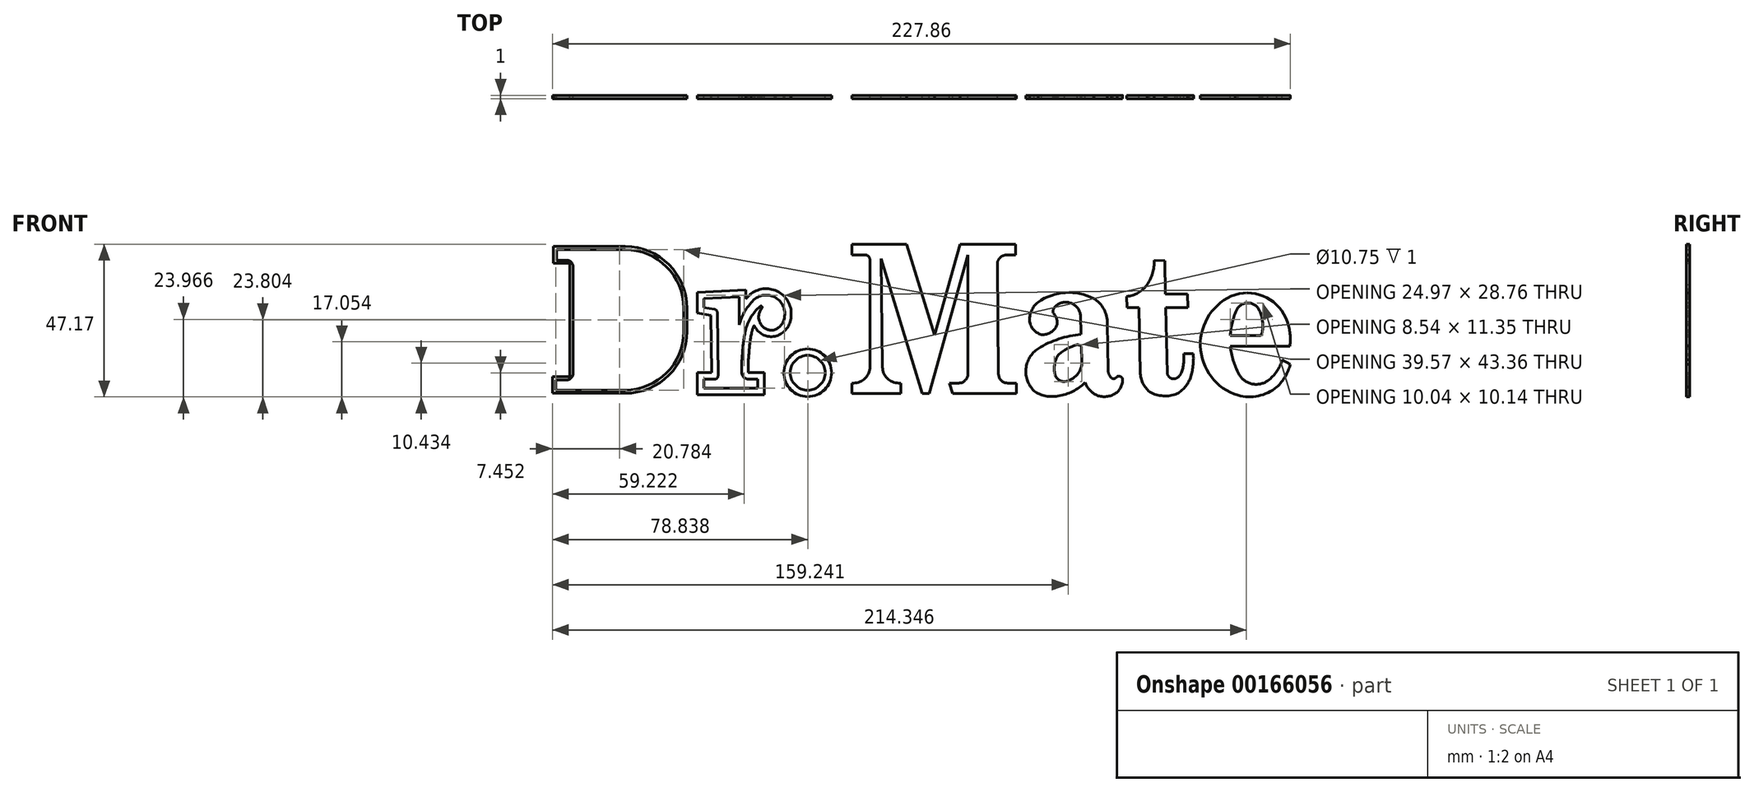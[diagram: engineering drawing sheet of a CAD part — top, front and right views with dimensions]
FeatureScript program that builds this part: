
annotation { "Feature Type Name" : "Feature", "Feature Type Description" : "" }
export const myFeature = defineFeature(function(context is Context, id is Id, definition is map)
    precondition{}
    {
        {
            var Q0;
            Q0=qCreatedBy(makeId("Front.planeOp"),FACE);
            var sketch = newSketch(context, id + "F0", { "sketchPlane" : qUnion([Q0])});
            skLineSegment(sketch, "E0", {"start": v(23.83, 45.48) * mm, "end": v(2.7, 45.48) * mm});
            skLineSegment(sketch, "E1", {"start": v(2.7, 45.48) * mm, "end": v(2.7, 42.24) * mm});
            skLineSegment(sketch, "E2", {"start": v(2.7, 42.24) * mm, "end": v(5.73, 42.24) * mm});
            skLineSegment(sketch, "E3", {"start": v(7.73, 40.24) * mm, "end": v(7.73, 7.24) * mm});
            skLineSegment(sketch, "E4", {"start": v(5.73, 5.24) * mm, "end": v(2.36, 5.24) * mm});
            skLineSegment(sketch, "E5", {"start": v(2.36, 5.24) * mm, "end": v(2.36, 2.11) * mm});
            skLineSegment(sketch, "E6", {"start": v(2.36, 2.11) * mm, "end": v(23.83, 2.11) * mm});
            skPoint(sketch, "E7.visualSharp", {"position": v(7.73, 42.24) * mm});
            skArc(sketch, "E7.filletArc", {"start": v(7.73, 40.24) * mm, "mid": v(7.14, 41.66) * mm, "end": v(5.73, 42.24) * mm});
            skPoint(sketch, "E8.visualSharp", {"position": v(7.73, 5.24) * mm});
            skArc(sketch, "E8.filletArc", {"start": v(5.73, 5.24) * mm, "mid": v(7.14, 5.83) * mm, "end": v(7.73, 7.24) * mm});
            skLineSegment(sketch, "E9", {"start": v(41.93, 27.38) * mm, "end": v(41.93, 20.21) * mm});
            skPoint(sketch, "E10.visualSharp", {"position": v(41.93, 45.48) * mm});
            skArc(sketch, "E10.filletArc", {"start": v(41.93, 27.38) * mm, "mid": v(36.63, 40.17) * mm, "end": v(23.83, 45.48) * mm});
            skPoint(sketch, "E11.visualSharp", {"position": v(41.93, 2.11) * mm});
            skArc(sketch, "E11.filletArc", {"start": v(23.83, 2.11) * mm, "mid": v(36.63, 7.41) * mm, "end": v(41.93, 20.21) * mm});
            skSolve(sketch);
        }
        {
            var Q0;
            Q0=qSketchRegion(id+"F0",true);
            extrude(context, id + "F1", {"entities" : qUnion([Q0]), "endBound" : BoundingType.SYMMETRIC, "depth" : 10 * mm});
        }
        {
            var Q0;
            Q0=qCreatedBy(makeId("Front.planeOp"),FACE);
            var sketch = newSketch(context, id + "F2", { "sketchPlane" : qUnion([Q0])});
            skLineSegment(sketch, "E12", {"start": v(20.26, 40.33) * mm, "end": v(20.26, 7.37) * mm});
            skLineSegment(sketch, "E13", {"start": v(22.26, 5.37) * mm, "end": v(23.68, 5.37) * mm});
            skLineSegment(sketch, "E14", {"start": v(22.26, 42.33) * mm, "end": v(23.68, 42.33) * mm});
            skPoint(sketch, "E15.visualSharp", {"position": v(20.26, 42.33) * mm});
            skArc(sketch, "E15.filletArc", {"start": v(22.26, 42.33) * mm, "mid": v(20.84, 41.75) * mm, "end": v(20.26, 40.33) * mm});
            skPoint(sketch, "E16.visualSharp", {"position": v(20.26, 5.37) * mm});
            skArc(sketch, "E16.filletArc", {"start": v(20.26, 7.37) * mm, "mid": v(20.84, 5.96) * mm, "end": v(22.26, 5.37) * mm});
            skPoint(sketch, "E17.visualSharp", {"position": v(41.68, 42.33) * mm});
            skArc(sketch, "E17.filletArc", {"start": v(29.92, 41.22) * mm, "mid": v(26.85, 42.05) * mm, "end": v(23.68, 42.33) * mm});
            skPoint(sketch, "E18.visualSharp", {"position": v(41.68, 5.37) * mm});
            skArc(sketch, "E18.filletArc", {"start": v(23.68, 5.37) * mm, "mid": v(26.85, 5.66) * mm, "end": v(29.92, 6.49) * mm});
            skArc(sketch, "E19", {"start": v(29.92, 6.49) * mm, "mid": v(31.56, 8.17) * mm, "end": v(33.02, 10) * mm});
            skArc(sketch, "E20.trimOffspring", {"start": v(33.02, 37.7) * mm, "mid": v(31.56, 39.54) * mm, "end": v(29.92, 41.22) * mm});
            skArc(sketch, "E21", {"start": v(33.02, 10) * mm, "mid": v(35.84, 23.85) * mm, "end": v(33.02, 37.7) * mm});
            skSolve(sketch);
        }
        {
            var Q0;
            Q0=qSketchRegion(id+"F2",true);
            extrude(context, id + "F3", {"entities" : qUnion([Q0]), "operationType" : NewBodyOperationType.REMOVE, "endBound" : BoundingType.SYMMETRIC, "oppositeDirection" : true, "depth" : 25 * mm});
        }
        {
            var Q0;
            Q0=makeQuery(id+"F3.boolean.opBoolean","COPY",EDGE,{"derivedFrom":makeQuery(id+"F3.opExtrude","SWEPT_EDGE",EDGE,{"disambiguationData":[OSD([sQuery(id+"F2.wireOp",EDGE,"E19"),sQuery(id+"F2.wireOp",EDGE,"E21")])]})});
            var Q1;
            Q1=makeQuery(id+"F3.boolean.opBoolean","COPY",EDGE,{"derivedFrom":makeQuery(id+"F3.opExtrude","SWEPT_EDGE",EDGE,{"disambiguationData":[OSD([sQuery(id+"F2.wireOp",EDGE,"E18.filletArc"),sQuery(id+"F2.wireOp",EDGE,"E19")])]})});
            var Q2;
            Q2=makeQuery(id+"F3.boolean.opBoolean","COPY",EDGE,{"derivedFrom":makeQuery(id+"F3.opExtrude","SWEPT_EDGE",EDGE,{"disambiguationData":[OSD([sQuery(id+"F2.wireOp",EDGE,"E20.trimOffspring"),sQuery(id+"F2.wireOp",EDGE,"E21")])]})});
            var Q3;
            Q3=makeQuery(id+"F3.boolean.opBoolean","COPY",EDGE,{"derivedFrom":makeQuery(id+"F3.opExtrude","SWEPT_EDGE",EDGE,{"disambiguationData":[OSD([sQuery(id+"F2.wireOp",EDGE,"E17.filletArc"),sQuery(id+"F2.wireOp",EDGE,"E20.trimOffspring")])]})});
            fillet(context, id + "F4", {"entities" : qUnion([Q0, Q1, Q2, Q3]), "radius" : 5 * mm, "tangentPropagation" : true, "allowEdgeOverflow" : false});
        }
        {
            var Q0;
            Q0=qCreatedBy(makeId("Front.planeOp"),FACE);
            var sketch = newSketch(context, id + "F5", { "sketchPlane" : qUnion([Q0])});
            skLineSegment(sketch, "E22", {"start": v(48.1, 30.42) * mm, "end": v(48.1, 27.61) * mm});
            skLineSegment(sketch, "E23", {"start": v(48.1, 30.42) * mm, "end": v(59.09, 30.93) * mm});
            skLineSegment(sketch, "E24", {"start": v(48.1, 2.66) * mm, "end": v(64.8, 2.66) * mm});
            skLineSegment(sketch, "E25", {"start": v(59.09, 30.93) * mm, "end": v(59.09, 22.2) * mm});
            skLineSegment(sketch, "E26", {"start": v(48.1, 5.47) * mm, "end": v(51.51, 5.47) * mm});
            skLineSegment(sketch, "E27", {"start": v(48.1, 27.61) * mm, "end": v(51.46, 27.04) * mm});
            skLineSegment(sketch, "E28", {"start": v(64.8, 5.47) * mm, "end": v(64.8, 2.66) * mm});
            skLineSegment(sketch, "E29.trimOffspring", {"start": v(52.29, 26.06) * mm, "end": v(52.51, 6.48) * mm});
            skLineSegment(sketch, "E30.trimOffspring", {"start": v(61.83, 5.47) * mm, "end": v(64.8, 5.47) * mm});
            skLineSegment(sketch, "E31.trimOffspring", {"start": v(48.1, 5.47) * mm, "end": v(48.1, 2.66) * mm});
            skArc(sketch, "E32", {"start": v(73.07, 24.94) * mm, "mid": v(70.3, 30.62) * mm, "end": v(64, 30.34) * mm});
            skArc(sketch, "E33", {"start": v(69.92, 20.7) * mm, "mid": v(72.14, 22.34) * mm, "end": v(73.07, 24.94) * mm});
            skArc(sketch, "E34", {"start": v(64, 30.34) * mm, "mid": v(60.9, 26.65) * mm, "end": v(59.09, 22.2) * mm});
            skArc(sketch, "E35", {"start": v(65.86, 22.25) * mm, "mid": v(67.65, 20.85) * mm, "end": v(69.92, 20.7) * mm});
            skArc(sketch, "E36", {"start": v(66.1, 27.52) * mm, "mid": v(65.06, 24.93) * mm, "end": v(65.86, 22.25) * mm});
            skArc(sketch, "E37", {"start": v(59.89, 6.98) * mm, "mid": v(60.62, 5.92) * mm, "end": v(61.83, 5.47) * mm});
            skArc(sketch, "E38", {"start": v(60.03, 13.08) * mm, "mid": v(59.8, 10.03) * mm, "end": v(59.89, 6.98) * mm});
            skArc(sketch, "E39", {"start": v(60.96, 20.37) * mm, "mid": v(60.34, 16.75) * mm, "end": v(60.03, 13.08) * mm});
            skArc(sketch, "E40", {"start": v(65.5, 27.94) * mm, "mid": v(62.63, 24.52) * mm, "end": v(60.96, 20.37) * mm});
            skArc(sketch, "E41", {"start": v(66.1, 27.52) * mm, "mid": v(65.98, 27.98) * mm, "end": v(65.5, 27.94) * mm});
            skPoint(sketch, "E42.visualSharp", {"position": v(52.28, 26.9) * mm});
            skArc(sketch, "E42.filletArc", {"start": v(52.29, 26.06) * mm, "mid": v(52.05, 26.7) * mm, "end": v(51.46, 27.04) * mm});
            skPoint(sketch, "E43.visualSharp", {"position": v(52.52, 5.47) * mm});
            skArc(sketch, "E43.filletArc", {"start": v(51.51, 5.47) * mm, "mid": v(52.22, 5.77) * mm, "end": v(52.51, 6.48) * mm});
            skSolve(sketch);
        }
        {
            var Q0;
            Q0=qSketchRegion(id+"F5",true);
            extrude(context, id + "F6", {"entities" : qUnion([Q0]), "endBound" : BoundingType.SYMMETRIC, "depth" : 10 * mm});
        }
        {
            var Q0;
            Q0=qCreatedBy(makeId("Front.planeOp"),FACE);
            var sketch = newSketch(context, id + "F7", { "sketchPlane" : qUnion([Q0])});
            skCircle(sketch, "E44", {"center": v(80.2, 7.44) * mm, "radius": 5.38 * mm});
            skSolve(sketch);
        }
        {
            var Q0;
            Q0=qSketchRegion(id+"F7",true);
            extrude(context, id + "F8", {"entities" : qUnion([Q0]), "endBound" : BoundingType.SYMMETRIC, "depth" : 10 * mm});
        }
        {
            var Q0;
            Q0=qCreatedBy(makeId("Front.planeOp"),FACE);
            var sketch = newSketch(context, id + "F9", { "sketchPlane" : qUnion([Q0])});
            skLineSegment(sketch, "E45", {"start": v(93.8, 47.16) * mm, "end": v(110.75, 47.16) * mm});
            skLineSegment(sketch, "E46", {"start": v(127.22, 47.16) * mm, "end": v(119.38, 19.02) * mm});
            skLineSegment(sketch, "E47", {"start": v(93.8, 47.16) * mm, "end": v(93.8, 43.88) * mm});
            skLineSegment(sketch, "E48", {"start": v(99.4, 42.37) * mm, "end": v(99.4, 9.27) * mm});
            skLineSegment(sketch, "E49", {"start": v(93.8, 1.02) * mm, "end": v(108.94, 1.02) * mm});
            skLineSegment(sketch, "E50", {"start": v(102.92, 42.74) * mm, "end": v(103.28, 9.22) * mm});
            skLineSegment(sketch, "E51", {"start": v(102.92, 42.74) * mm, "end": v(115.57, 1.02) * mm});
            skLineSegment(sketch, "E52", {"start": v(110.75, 47.16) * mm, "end": v(119.38, 19.02) * mm});
            skLineSegment(sketch, "E53", {"start": v(129.69, 43.89) * mm, "end": v(129.69, 7.07) * mm});
            skLineSegment(sketch, "E54", {"start": v(138.75, 40.98) * mm, "end": v(139.12, 7.04) * mm});
            skLineSegment(sketch, "E55", {"start": v(144.36, 47.16) * mm, "end": v(144.39, 43.8) * mm});
            skLineSegment(sketch, "E56", {"start": v(93.8, 43.88) * mm, "end": v(97.9, 43.87) * mm});
            skLineSegment(sketch, "E57.0", {"start": v(93.8, 4.27) * mm, "end": v(94.4, 4.27) * mm});
            skPoint(sketch, "E58.orphan", {"position": v(90.95, 43.89) * mm});
            skPoint(sketch, "E59.orphan", {"position": v(90.95, 47.16) * mm});
            skLineSegment(sketch, "E60.trimOffspring", {"start": v(144.68, 4.27) * mm, "end": v(144.7, 1.02) * mm});
            skLineSegment(sketch, "E61.trimOffspring", {"start": v(141.56, 43.8) * mm, "end": v(144.39, 43.8) * mm});
            skLineSegment(sketch, "E62.trimOffspring", {"start": v(127.22, 47.16) * mm, "end": v(144.36, 47.16) * mm});
            skLineSegment(sketch, "E63.trimOffspring", {"start": v(93.8, 4.27) * mm, "end": v(93.8, 1.02) * mm});
            skLineSegment(sketch, "E64.trimOffspring", {"start": v(117.74, 1.02) * mm, "end": v(129.69, 43.89) * mm});
            skLineSegment(sketch, "E65.trimOffspring", {"start": v(123.9, 4.27) * mm, "end": v(124.9, 1.02) * mm});
            skLineSegment(sketch, "E66.trimOffspring", {"start": v(108.28, 4.27) * mm, "end": v(108.96, 4.27) * mm});
            skLineSegment(sketch, "E67.trimOffspring", {"start": v(123.9, 4.27) * mm, "end": v(126.89, 4.27) * mm});
            skLineSegment(sketch, "E68.trimOffspring", {"start": v(124.9, 1.02) * mm, "end": v(144.7, 1.02) * mm});
            skLineSegment(sketch, "E69.trimOffspring", {"start": v(141.92, 4.27) * mm, "end": v(144.68, 4.27) * mm});
            skPoint(sketch, "E70.startSnap0", {"position": v(108.96, 4.27) * mm});
            skLineSegment(sketch, "E71", {"start": v(108.94, 4.27) * mm, "end": v(108.94, 1.02) * mm});
            skLineSegment(sketch, "E72.trimOffspring", {"start": v(115.57, 1.02) * mm, "end": v(117.74, 1.02) * mm});
            skPoint(sketch, "E73.visualSharp", {"position": v(99.4, 43.87) * mm});
            skArc(sketch, "E73.filletArc", {"start": v(99.4, 42.37) * mm, "mid": v(98.96, 43.43) * mm, "end": v(97.9, 43.87) * mm});
            skPoint(sketch, "E74.visualSharp", {"position": v(99.4, 4.27) * mm});
            skArc(sketch, "E74.filletArc", {"start": v(94.4, 4.27) * mm, "mid": v(97.94, 5.74) * mm, "end": v(99.4, 9.27) * mm});
            skPoint(sketch, "E75.visualSharp", {"position": v(103.34, 4.27) * mm});
            skArc(sketch, "E75.filletArc", {"start": v(103.28, 9.22) * mm, "mid": v(104.77, 5.72) * mm, "end": v(108.28, 4.27) * mm});
            skPoint(sketch, "E76.visualSharp", {"position": v(129.69, 4.27) * mm});
            skArc(sketch, "E76.filletArc", {"start": v(126.89, 4.27) * mm, "mid": v(128.87, 5.1) * mm, "end": v(129.69, 7.07) * mm});
            skPoint(sketch, "E77.visualSharp", {"position": v(139.15, 4.27) * mm});
            skArc(sketch, "E77.filletArc", {"start": v(139.12, 7.04) * mm, "mid": v(139.95, 5.08) * mm, "end": v(141.92, 4.27) * mm});
            skPoint(sketch, "E78.visualSharp", {"position": v(138.72, 43.81) * mm});
            skArc(sketch, "E78.filletArc", {"start": v(141.56, 43.8) * mm, "mid": v(139.56, 42.98) * mm, "end": v(138.75, 40.98) * mm});
            skSolve(sketch);
        }
        {
            var Q0;
            Q0=qSketchRegion(id+"F9",true);
            extrude(context, id + "F10", {"entities" : qUnion([Q0]), "endBound" : BoundingType.SYMMETRIC, "depth" : 1 * mm});
        }
        {
            var Q0;
            Q0=qCreatedBy(makeId("Front.planeOp"),FACE);
            var sketch = newSketch(context, id + "F11", { "sketchPlane" : qUnion([Q0])});
            skArc(sketch, "E79", {"start": v(172.7, 22.65) * mm, "mid": v(171.66, 27.12) * mm, "end": v(168.48, 30.43) * mm});
            skLineSegment(sketch, "E80", {"start": v(172.7, 22.65) * mm, "end": v(172.93, 8.42) * mm});
            skArc(sketch, "E81", {"start": v(168.48, 30.43) * mm, "mid": v(159.76, 32.2) * mm, "end": v(151.36, 29.26) * mm});
            skArc(sketch, "E82", {"start": v(151.36, 29.26) * mm, "mid": v(149.3, 26.59) * mm, "end": v(148.75, 23.26) * mm});
            skArc(sketch, "E83", {"start": v(148.75, 23.26) * mm, "mid": v(149.95, 20.7) * mm, "end": v(152.36, 19.26) * mm});
            skArc(sketch, "E84", {"start": v(152.36, 19.26) * mm, "mid": v(155.23, 19.9) * mm, "end": v(157.14, 22.15) * mm});
            skArc(sketch, "E85", {"start": v(157.14, 22.15) * mm, "mid": v(157.07, 24.2) * mm, "end": v(155.97, 25.93) * mm});
            skArc(sketch, "E86", {"start": v(156.97, 28.2) * mm, "mid": v(156.13, 27.22) * mm, "end": v(155.97, 25.93) * mm});
            skArc(sketch, "E87", {"start": v(164.45, 25.33) * mm, "mid": v(161.55, 28.93) * mm, "end": v(156.97, 28.2) * mm});
            skLineSegment(sketch, "E88", {"start": v(164.45, 25.33) * mm, "end": v(164.87, 11.05) * mm});
            skArc(sketch, "E89", {"start": v(164.74, 15.46) * mm, "mid": v(164.18, 15.94) * mm, "end": v(163.46, 16.1) * mm});
            skArc(sketch, "E90", {"start": v(164.63, 19.28) * mm, "mid": v(157.74, 17.88) * mm, "end": v(151.36, 14.93) * mm});
            skArc(sketch, "E91", {"start": v(151.36, 14.93) * mm, "mid": v(147.6, 8.68) * mm, "end": v(150.1, 1.82) * mm});
            skArc(sketch, "E92", {"start": v(150.1, 1.82) * mm, "mid": v(153.65, 0.29) * mm, "end": v(157.51, 0.28) * mm});
            skArc(sketch, "E93", {"start": v(157.51, 0.28) * mm, "mid": v(162.02, 1.68) * mm, "end": v(165.85, 4.44) * mm});
            skArc(sketch, "E94", {"start": v(159.52, 4.75) * mm, "mid": v(163.4, 6.87) * mm, "end": v(164.87, 11.05) * mm});
            skArc(sketch, "E95", {"start": v(156.5, 7.23) * mm, "mid": v(157.54, 5.41) * mm, "end": v(159.52, 4.75) * mm});
            skArc(sketch, "E96", {"start": v(157.54, 12.92) * mm, "mid": v(156.46, 10.18) * mm, "end": v(156.5, 7.23) * mm});
            skPoint(sketch, "E96.startSnap0", {"position": v(157.54, 5.41) * mm});
            skArc(sketch, "E97", {"start": v(163.46, 16.1) * mm, "mid": v(160.31, 14.86) * mm, "end": v(157.54, 12.92) * mm});
            skArc(sketch, "E98", {"start": v(172.93, 8.42) * mm, "mid": v(173.22, 7) * mm, "end": v(174.02, 5.8) * mm});
            skArc(sketch, "E99", {"start": v(174.02, 5.8) * mm, "mid": v(174.98, 5.66) * mm, "end": v(175.7, 6.3) * mm});
            skArc(sketch, "E100", {"start": v(177.42, 5.6) * mm, "mid": v(176.71, 6.32) * mm, "end": v(175.7, 6.3) * mm});
            skArc(sketch, "E101", {"start": v(174.62, 0.74) * mm, "mid": v(176.77, 2.73) * mm, "end": v(177.42, 5.6) * mm});
            skArc(sketch, "E102", {"start": v(165.85, 4.44) * mm, "mid": v(167.1, 2.35) * mm, "end": v(168.94, 0.77) * mm});
            skArc(sketch, "E103", {"start": v(168.94, 0.77) * mm, "mid": v(171.78, 0.05) * mm, "end": v(174.62, 0.74) * mm});
            skSolve(sketch);
        }
        {
            var Q0;
            Q0=qSketchRegion(id+"F11",true);
            extrude(context, id + "F12", {"entities" : qUnion([Q0]), "endBound" : BoundingType.SYMMETRIC, "depth" : 1 * mm});
        }
        {
            var Q0;
            Q0=qCreatedBy(makeId("Front.planeOp"),FACE);
            var sketch = newSketch(context, id + "F13", { "sketchPlane" : qUnion([Q0])});
            skLineSegment(sketch, "E104", {"start": v(187.18, 42.16) * mm, "end": v(190.44, 42.1) * mm});
            skLineSegment(sketch, "E105", {"start": v(190.44, 42.1) * mm, "end": v(190.67, 31.73) * mm});
            skLineSegment(sketch, "E106", {"start": v(178.8, 27.63) * mm, "end": v(182.53, 27.63) * mm});
            skLineSegment(sketch, "E107", {"start": v(197.44, 31.73) * mm, "end": v(190.67, 31.73) * mm});
            skLineSegment(sketch, "E108", {"start": v(178.7, 31.04) * mm, "end": v(178.8, 27.63) * mm});
            skLineSegment(sketch, "E109", {"start": v(197.44, 31.73) * mm, "end": v(197.59, 27.63) * mm});
            skLineSegment(sketch, "E110", {"start": v(196.3, 13.37) * mm, "end": v(199.27, 13.37) * mm});
            skArc(sketch, "E111", {"start": v(182.9, 7.56) * mm, "mid": v(183.7, 4.23) * mm, "end": v(185.78, 1.52) * mm});
            skArc(sketch, "E112", {"start": v(185.78, 1.52) * mm, "mid": v(189.97, 0.3) * mm, "end": v(194.28, 0.99) * mm});
            skArc(sketch, "E113", {"start": v(194.28, 0.99) * mm, "mid": v(196.72, 3.04) * mm, "end": v(198.37, 5.77) * mm});
            skArc(sketch, "E114", {"start": v(198.37, 5.77) * mm, "mid": v(199.19, 9.53) * mm, "end": v(199.27, 13.37) * mm});
            skArc(sketch, "E115", {"start": v(191.2, 7.87) * mm, "mid": v(191.86, 6.09) * mm, "end": v(193.7, 5.6) * mm});
            skArc(sketch, "E116", {"start": v(193.7, 5.6) * mm, "mid": v(194.65, 6.17) * mm, "end": v(195.36, 7.01) * mm});
            skArc(sketch, "E117", {"start": v(195.36, 7.01) * mm, "mid": v(196.26, 10.12) * mm, "end": v(196.3, 13.37) * mm});
            skLineSegment(sketch, "E118.trimOffspring", {"start": v(190.76, 27.63) * mm, "end": v(197.59, 27.63) * mm});
            skLineSegment(sketch, "E119.trimOffspring", {"start": v(182.53, 27.63) * mm, "end": v(182.9, 7.56) * mm});
            skLineSegment(sketch, "E120.trimOffspring", {"start": v(190.76, 27.63) * mm, "end": v(191.22, 7.26) * mm});
            skPoint(sketch, "E121.visualSharp", {"position": v(182.26, 42.25) * mm});
            skArc(sketch, "E122", {"start": v(178.7, 31.04) * mm, "mid": v(182.27, 32.15) * mm, "end": v(185, 34.71) * mm});
            skArc(sketch, "E123", {"start": v(185, 34.71) * mm, "mid": v(186.7, 38.26) * mm, "end": v(187.18, 42.16) * mm});
            skSolve(sketch);
        }
        {
            var Q0;
            Q0=qSketchRegion(id+"F13",true);
            extrude(context, id + "F14", {"entities" : qUnion([Q0]), "endBound" : BoundingType.SYMMETRIC, "depth" : 1 * mm});
        }
        {
            var Q0;
            Q0=qCreatedBy(makeId("Front.planeOp"),FACE);
            var sketch = newSketch(context, id + "F15", { "sketchPlane" : qUnion([Q0])});
            skLineSegment(sketch, "E124", {"start": v(210.69, 18.89) * mm, "end": v(220.1, 18.89) * mm});
            skLineSegment(sketch, "E125", {"start": v(210.74, 15.7) * mm, "end": v(229.12, 15.7) * mm});
            skLineSegment(sketch, "E126", {"start": v(226.7, 11.4) * mm, "end": v(229.2, 10.1) * mm});
            skArc(sketch, "E127", {"start": v(212.17, 31.58) * mm, "mid": v(201.46, 15.7) * mm, "end": v(213.05, 0.47) * mm});
            skArc(sketch, "E128", {"start": v(228.31, 23.2) * mm, "mid": v(221.93, 30.65) * mm, "end": v(212.17, 31.58) * mm});
            skArc(sketch, "E129.trimOffspring", {"start": v(229.12, 15.7) * mm, "mid": v(229.12, 19.5) * mm, "end": v(228.31, 23.2) * mm});
            skArc(sketch, "E130", {"start": v(219.75, 26.59) * mm, "mid": v(216.18, 29.03) * mm, "end": v(212.55, 26.67) * mm});
            skArc(sketch, "E131", {"start": v(220.58, 20.03) * mm, "mid": v(220.63, 23.37) * mm, "end": v(219.75, 26.59) * mm});
            skArc(sketch, "E132", {"start": v(220.1, 18.89) * mm, "mid": v(220.37, 19.45) * mm, "end": v(220.58, 20.03) * mm});
            skArc(sketch, "E133", {"start": v(213.05, 0.47) * mm, "mid": v(219.37, 0.28) * mm, "end": v(225.06, 3.02) * mm});
            skArc(sketch, "E134", {"start": v(225.06, 3.02) * mm, "mid": v(227.65, 6.26) * mm, "end": v(229.2, 10.1) * mm});
            skArc(sketch, "E135", {"start": v(213.34, 7.06) * mm, "mid": v(217.36, 4.02) * mm, "end": v(222.3, 5.01) * mm});
            skArc(sketch, "E136", {"start": v(222.3, 5.01) * mm, "mid": v(225.03, 7.85) * mm, "end": v(226.7, 11.4) * mm});
            skArc(sketch, "E137", {"start": v(212.55, 26.67) * mm, "mid": v(211.27, 22.86) * mm, "end": v(210.69, 18.89) * mm});
            skArc(sketch, "E138.trimOffspring", {"start": v(210.74, 15.7) * mm, "mid": v(211.6, 11.25) * mm, "end": v(213.34, 7.06) * mm});
            skSolve(sketch);
        }
        {
            var Q0;
            Q0=qSketchRegion(id+"F15",true);
            extrude(context, id + "F16", {"entities" : qUnion([Q0]), "endBound" : BoundingType.SYMMETRIC, "depth" : 1 * mm});
        }
        {
            var Q0;
            Q0=qCreatedBy(makeId("Front.planeOp"),FACE);
            var sketch = newSketch(context, id + "F17", { "sketchPlane" : qUnion([Q0])});
            skLineSegment(sketch, "E139.0", {"start": v(22.26, 42.33) * mm, "end": v(23.68, 42.33) * mm});
            skArc(sketch, "E139.1", {"start": v(28.62, 41.64) * mm, "mid": v(29.82, 41.12) * mm, "end": v(30.85, 40.3) * mm});
            skArc(sketch, "E139.2", {"start": v(30.85, 7.4) * mm, "mid": v(29.82, 6.59) * mm, "end": v(28.62, 6.07) * mm});
            skArc(sketch, "E139.3", {"start": v(5.73, 5.24) * mm, "mid": v(7.14, 5.83) * mm, "end": v(7.73, 7.24) * mm});
            skArc(sketch, "E139.4", {"start": v(41.93, 27.38) * mm, "mid": v(36.63, 40.17) * mm, "end": v(23.83, 45.48) * mm});
            skArc(sketch, "E139.5", {"start": v(23.83, 2.11) * mm, "mid": v(36.63, 7.41) * mm, "end": v(41.93, 20.21) * mm});
            skArc(sketch, "E139.6", {"start": v(22.26, 42.33) * mm, "mid": v(20.84, 41.75) * mm, "end": v(20.26, 40.33) * mm});
            skArc(sketch, "E139.7", {"start": v(28.62, 41.64) * mm, "mid": v(26.18, 42.16) * mm, "end": v(23.68, 42.33) * mm});
            skArc(sketch, "E139.8", {"start": v(30.85, 7.4) * mm, "mid": v(31.76, 8.4) * mm, "end": v(32.6, 9.45) * mm});
            skArc(sketch, "E139.9", {"start": v(32.6, 38.26) * mm, "mid": v(31.76, 39.3) * mm, "end": v(30.85, 40.3) * mm});
            skArc(sketch, "E139.10", {"start": v(33.28, 10.63) * mm, "mid": v(35.84, 23.85) * mm, "end": v(33.28, 37.08) * mm});
            skArc(sketch, "E139.11", {"start": v(23.68, 5.37) * mm, "mid": v(26.18, 5.55) * mm, "end": v(28.62, 6.07) * mm});
            skLineSegment(sketch, "E139.12", {"start": v(23.83, 45.48) * mm, "end": v(2.7, 45.48) * mm});
            skLineSegment(sketch, "E139.13", {"start": v(2.7, 45.48) * mm, "end": v(2.7, 42.24) * mm});
            skLineSegment(sketch, "E139.16", {"start": v(22.26, 5.37) * mm, "end": v(23.68, 5.37) * mm});
            skLineSegment(sketch, "E139.20", {"start": v(20.26, 40.33) * mm, "end": v(20.26, 7.37) * mm});
            skArc(sketch, "E139.22", {"start": v(32.6, 38.26) * mm, "mid": v(32.98, 37.7) * mm, "end": v(33.28, 37.08) * mm});
            skArc(sketch, "E139.25", {"start": v(30.85, 40.3) * mm, "mid": v(29.82, 41.12) * mm, "end": v(28.62, 41.64) * mm});
            skArc(sketch, "E139.28", {"start": v(33.28, 10.63) * mm, "mid": v(32.98, 10.01) * mm, "end": v(32.6, 9.45) * mm});
            skLineSegment(sketch, "E139.29", {"start": v(41.93, 27.38) * mm, "end": v(41.93, 20.21) * mm});
            skArc(sketch, "E139.30", {"start": v(41.93, 27.38) * mm, "mid": v(36.63, 40.17) * mm, "end": v(23.83, 45.48) * mm});
            skLineSegment(sketch, "E139.31", {"start": v(2.7, 42.24) * mm, "end": v(5.73, 42.24) * mm});
            skArc(sketch, "E139.32", {"start": v(23.83, 2.11) * mm, "mid": v(36.63, 7.41) * mm, "end": v(41.93, 20.21) * mm});
            skLineSegment(sketch, "E139.33", {"start": v(7.73, 40.24) * mm, "end": v(7.73, 7.24) * mm});
            skLineSegment(sketch, "E139.34", {"start": v(5.73, 5.24) * mm, "end": v(2.36, 5.24) * mm});
            skLineSegment(sketch, "E139.35", {"start": v(2.36, 5.24) * mm, "end": v(2.36, 2.11) * mm});
            skLineSegment(sketch, "E139.36", {"start": v(2.36, 2.11) * mm, "end": v(23.83, 2.11) * mm});
            skArc(sketch, "E139.37", {"start": v(7.73, 40.24) * mm, "mid": v(7.14, 41.66) * mm, "end": v(5.73, 42.24) * mm});
            skArc(sketch, "E139.38", {"start": v(22.26, 42.33) * mm, "mid": v(20.84, 41.75) * mm, "end": v(20.26, 40.33) * mm});
            skArc(sketch, "E139.39", {"start": v(20.26, 7.37) * mm, "mid": v(20.84, 5.96) * mm, "end": v(22.26, 5.37) * mm});
            skArc(sketch, "E139.40", {"start": v(32.6, 38.26) * mm, "mid": v(31.76, 39.3) * mm, "end": v(30.85, 40.3) * mm});
            skArc(sketch, "E139.41", {"start": v(33.28, 10.63) * mm, "mid": v(35.84, 23.85) * mm, "end": v(33.28, 37.08) * mm});
            skLineSegment(sketch, "E139.42", {"start": v(2.7, 45.48) * mm, "end": v(2.7, 42.24) * mm});
            skLineSegment(sketch, "E139.53", {"start": v(23.83, 45.48) * mm, "end": v(2.7, 45.48) * mm});
            skLineSegment(sketch, "E139.54", {"start": v(22.26, 42.33) * mm, "end": v(23.68, 42.33) * mm});
            skLineSegment(sketch, "E139.58", {"start": v(20.26, 40.33) * mm, "end": v(20.26, 7.37) * mm});
            skLineSegment(sketch, "E139.59", {"start": v(22.26, 5.37) * mm, "end": v(23.68, 5.37) * mm});
            skArc(sketch, "E139.60", {"start": v(28.62, 6.07) * mm, "mid": v(29.82, 6.59) * mm, "end": v(30.85, 7.4) * mm});
            skLineSegment(sketch, "E139.64", {"start": v(41.93, 27.38) * mm, "end": v(41.93, 20.21) * mm});
            skLineSegment(sketch, "E139.65", {"start": v(2.7, 42.24) * mm, "end": v(5.73, 42.24) * mm});
            skLineSegment(sketch, "E139.66", {"start": v(7.73, 40.24) * mm, "end": v(7.73, 7.24) * mm});
            skLineSegment(sketch, "E139.67", {"start": v(5.73, 5.24) * mm, "end": v(2.36, 5.24) * mm});
            skLineSegment(sketch, "E139.68", {"start": v(2.36, 5.24) * mm, "end": v(2.36, 2.11) * mm});
            skLineSegment(sketch, "E139.69", {"start": v(2.36, 2.11) * mm, "end": v(23.83, 2.11) * mm});
            skArc(sketch, "E139.70", {"start": v(5.73, 5.24) * mm, "mid": v(7.14, 5.83) * mm, "end": v(7.73, 7.24) * mm});
            skArc(sketch, "E139.71", {"start": v(20.26, 7.37) * mm, "mid": v(20.84, 5.96) * mm, "end": v(22.26, 5.37) * mm});
            skArc(sketch, "E139.72", {"start": v(28.62, 41.64) * mm, "mid": v(26.18, 42.16) * mm, "end": v(23.68, 42.33) * mm});
            skArc(sketch, "E139.73", {"start": v(30.85, 7.4) * mm, "mid": v(31.76, 8.4) * mm, "end": v(32.6, 9.45) * mm});
            skArc(sketch, "E139.74", {"start": v(23.68, 5.37) * mm, "mid": v(26.18, 5.55) * mm, "end": v(28.62, 6.07) * mm});
            skArc(sketch, "E139.75", {"start": v(33.28, 37.08) * mm, "mid": v(32.98, 37.7) * mm, "end": v(32.6, 38.26) * mm});
            skArc(sketch, "E139.76", {"start": v(32.6, 9.45) * mm, "mid": v(32.98, 10.01) * mm, "end": v(33.28, 10.63) * mm});
            skArc(sketch, "E139.77", {"start": v(7.73, 40.24) * mm, "mid": v(7.14, 41.66) * mm, "end": v(5.73, 42.24) * mm});
            skLineSegment(sketch, "E140.0", {"start": v(22.26, 40.33) * mm, "end": v(22.26, 7.37) * mm});
            skLineSegment(sketch, "E141.0", {"start": v(22.26, 7.37) * mm, "end": v(23.68, 7.37) * mm});
            skArc(sketch, "E141.1", {"start": v(23.68, 7.37) * mm, "mid": v(26.3, 7.6) * mm, "end": v(28.85, 8.23) * mm});
            skArc(sketch, "E141.2", {"start": v(28.85, 8.23) * mm, "mid": v(30.12, 9.56) * mm, "end": v(31.27, 11) * mm});
            skLineSegment(sketch, "E141.3", {"start": v(22.26, 40.33) * mm, "end": v(23.68, 40.33) * mm});
            skArc(sketch, "E141.4", {"start": v(28.85, 39.47) * mm, "mid": v(26.3, 40.12) * mm, "end": v(23.68, 40.33) * mm});
            skArc(sketch, "E141.5", {"start": v(31.27, 36.71) * mm, "mid": v(30.12, 38.14) * mm, "end": v(28.85, 39.47) * mm});
            skArc(sketch, "E141.6", {"start": v(31.27, 11) * mm, "mid": v(33.84, 23.85) * mm, "end": v(31.27, 36.71) * mm});
            skLineSegment(sketch, "E142.0", {"start": v(23.83, 46.48) * mm, "end": v(1.7, 46.48) * mm});
            skArc(sketch, "E142.1", {"start": v(42.93, 27.38) * mm, "mid": v(37.33, 40.88) * mm, "end": v(23.83, 46.48) * mm});
            skLineSegment(sketch, "E142.2", {"start": v(1.7, 46.48) * mm, "end": v(1.7, 41.24) * mm});
            skLineSegment(sketch, "E142.3", {"start": v(42.93, 27.38) * mm, "end": v(42.93, 20.21) * mm});
            skArc(sketch, "E142.4", {"start": v(23.83, 1.11) * mm, "mid": v(37.33, 6.7) * mm, "end": v(42.93, 20.21) * mm});
            skLineSegment(sketch, "E142.5", {"start": v(1.36, 1.11) * mm, "end": v(23.83, 1.11) * mm});
            skLineSegment(sketch, "E142.6", {"start": v(1.7, 41.24) * mm, "end": v(6.73, 41.24) * mm});
            skLineSegment(sketch, "E142.7", {"start": v(6.73, 41.24) * mm, "end": v(6.73, 6.24) * mm});
            skLineSegment(sketch, "E142.8", {"start": v(6.73, 6.24) * mm, "end": v(1.36, 6.24) * mm});
            skLineSegment(sketch, "E142.9", {"start": v(1.36, 6.24) * mm, "end": v(1.36, 1.11) * mm});
            skArc(sketch, "E143.0", {"start": v(40.93, 27.38) * mm, "mid": v(35.92, 39.47) * mm, "end": v(23.83, 44.48) * mm});
            skLineSegment(sketch, "E143.1", {"start": v(8.73, 40.24) * mm, "end": v(8.73, 7.24) * mm});
            skArc(sketch, "E143.2", {"start": v(8.73, 40.24) * mm, "mid": v(7.85, 42.36) * mm, "end": v(5.73, 43.24) * mm});
            skLineSegment(sketch, "E143.3", {"start": v(3.7, 43.24) * mm, "end": v(5.73, 43.24) * mm});
            skLineSegment(sketch, "E143.4", {"start": v(3.7, 44.48) * mm, "end": v(3.7, 43.24) * mm});
            skArc(sketch, "E143.5", {"start": v(5.73, 4.24) * mm, "mid": v(7.85, 5.12) * mm, "end": v(8.73, 7.24) * mm});
            skLineSegment(sketch, "E143.6", {"start": v(23.83, 44.48) * mm, "end": v(3.7, 44.48) * mm});
            skLineSegment(sketch, "E143.7", {"start": v(5.73, 4.24) * mm, "end": v(3.36, 4.24) * mm});
            skLineSegment(sketch, "E143.8", {"start": v(3.36, 4.24) * mm, "end": v(3.36, 3.11) * mm});
            skLineSegment(sketch, "E143.9", {"start": v(3.36, 3.11) * mm, "end": v(23.83, 3.11) * mm});
            skArc(sketch, "E143.10", {"start": v(23.83, 3.11) * mm, "mid": v(35.92, 8.12) * mm, "end": v(40.93, 20.21) * mm});
            skLineSegment(sketch, "E143.11", {"start": v(40.93, 27.38) * mm, "end": v(40.93, 20.21) * mm});
            skSolve(sketch);
        }
        {
            var Q0;
            Q0=qSketchRegion(id+"F17",true);
            var Q1;
            Q1=makeQuery(id+"F17.imprint","IMPRINT",FACE,{"disambiguationData":[TD([[makeQuery(id+"F17.imprint","IMPRINT",EDGE,{"derivedFrom":sQuery(id+"F17.wireOp",EDGE,"E139.30")}),1.0]])]});
            var Q2;
            Q2=makeQuery(id+"F17.imprint","IMPRINT",FACE,{"disambiguationData":[TD([[makeQuery(id+"F17.imprint","IMPRINT",EDGE,{"derivedFrom":sQuery(id+"F17.wireOp",EDGE,"E139.25")}),1.0]])]});
            extrude(context, id + "F18", {"entities" : qUnion([Q0, Q1, Q2]), "endBound" : BoundingType.SYMMETRIC, "depth" : 1 * mm});
        }
        {
            var Q0;
            Q0=qCreatedBy(makeId("Front.planeOp"),FACE);
            var sketch = newSketch(context, id + "F19", { "sketchPlane" : qUnion([Q0])});
            skArc(sketch, "E144.0", {"start": v(65.5, 27.94) * mm, "mid": v(62.63, 24.52) * mm, "end": v(60.96, 20.37) * mm});
            skArc(sketch, "E144.1", {"start": v(60.96, 20.37) * mm, "mid": v(60.34, 16.75) * mm, "end": v(60.03, 13.08) * mm});
            skArc(sketch, "E144.2", {"start": v(60.03, 13.08) * mm, "mid": v(59.8, 10.03) * mm, "end": v(59.89, 6.98) * mm});
            skArc(sketch, "E144.3", {"start": v(65.86, 22.25) * mm, "mid": v(67.65, 20.85) * mm, "end": v(69.92, 20.7) * mm});
            skArc(sketch, "E144.4", {"start": v(66.1, 27.52) * mm, "mid": v(65.06, 24.93) * mm, "end": v(65.86, 22.25) * mm});
            skArc(sketch, "E144.5", {"start": v(59.89, 6.98) * mm, "mid": v(60.62, 5.92) * mm, "end": v(61.83, 5.47) * mm});
            skLineSegment(sketch, "E144.6", {"start": v(48.1, 30.42) * mm, "end": v(48.1, 27.61) * mm});
            skLineSegment(sketch, "E144.7", {"start": v(48.1, 30.42) * mm, "end": v(59.09, 30.93) * mm});
            skLineSegment(sketch, "E144.8", {"start": v(48.1, 2.66) * mm, "end": v(64.8, 2.66) * mm});
            skLineSegment(sketch, "E144.9", {"start": v(59.09, 30.93) * mm, "end": v(59.09, 22.2) * mm});
            skLineSegment(sketch, "E144.10", {"start": v(48.1, 5.47) * mm, "end": v(51.51, 5.47) * mm});
            skLineSegment(sketch, "E144.11", {"start": v(48.1, 27.61) * mm, "end": v(51.46, 27.04) * mm});
            skLineSegment(sketch, "E144.12", {"start": v(64.8, 5.47) * mm, "end": v(64.8, 2.66) * mm});
            skLineSegment(sketch, "E144.13", {"start": v(52.29, 26.06) * mm, "end": v(52.51, 6.48) * mm});
            skLineSegment(sketch, "E144.14", {"start": v(61.83, 5.47) * mm, "end": v(64.8, 5.47) * mm});
            skLineSegment(sketch, "E144.15", {"start": v(48.1, 5.47) * mm, "end": v(48.1, 2.66) * mm});
            skArc(sketch, "E144.16", {"start": v(73.07, 24.94) * mm, "mid": v(70.3, 30.62) * mm, "end": v(64, 30.34) * mm});
            skArc(sketch, "E144.17", {"start": v(69.92, 20.7) * mm, "mid": v(72.14, 22.34) * mm, "end": v(73.07, 24.94) * mm});
            skArc(sketch, "E144.18", {"start": v(64, 30.34) * mm, "mid": v(60.9, 26.65) * mm, "end": v(59.09, 22.2) * mm});
            skArc(sketch, "E144.19", {"start": v(51.51, 5.47) * mm, "mid": v(52.22, 5.77) * mm, "end": v(52.51, 6.48) * mm});
            skArc(sketch, "E144.20", {"start": v(66.1, 27.52) * mm, "mid": v(65.98, 27.98) * mm, "end": v(65.5, 27.94) * mm});
            skArc(sketch, "E144.21", {"start": v(52.29, 26.06) * mm, "mid": v(52.05, 26.7) * mm, "end": v(51.46, 27.04) * mm});
            skArc(sketch, "E145.0", {"start": v(63.63, 22.11) * mm, "mid": v(63.9, 21.59) * mm, "end": v(64.23, 21.09) * mm});
            skArc(sketch, "E145.1", {"start": v(63.63, 22.11) * mm, "mid": v(63.22, 21.04) * mm, "end": v(62.91, 19.94) * mm});
            skArc(sketch, "E145.2", {"start": v(62.91, 19.94) * mm, "mid": v(62.32, 16.45) * mm, "end": v(62.03, 12.92) * mm});
            skArc(sketch, "E145.3", {"start": v(62.03, 12.92) * mm, "mid": v(61.81, 10.21) * mm, "end": v(61.86, 7.5) * mm});
            skArc(sketch, "E145.4", {"start": v(61.86, 7.5) * mm, "mid": v(61.89, 7.48) * mm, "end": v(61.92, 7.47) * mm});
            skArc(sketch, "E145.5", {"start": v(64.23, 21.09) * mm, "mid": v(67, 18.96) * mm, "end": v(70.48, 18.78) * mm});
            skLineSegment(sketch, "E145.6", {"start": v(61.92, 7.47) * mm, "end": v(66.8, 7.47) * mm});
            skLineSegment(sketch, "E145.7", {"start": v(66.8, 7.47) * mm, "end": v(66.8, 0.66) * mm});
            skLineSegment(sketch, "E145.8", {"start": v(46.1, 0.66) * mm, "end": v(66.8, 0.66) * mm});
            skLineSegment(sketch, "E145.9", {"start": v(61.09, 33.03) * mm, "end": v(61.09, 30.26) * mm});
            skArc(sketch, "E145.10", {"start": v(62.74, 31.9) * mm, "mid": v(61.89, 31.1) * mm, "end": v(61.09, 30.26) * mm});
            skArc(sketch, "E145.11", {"start": v(75.06, 24.77) * mm, "mid": v(71.24, 32.39) * mm, "end": v(62.74, 31.9) * mm});
            skArc(sketch, "E145.12", {"start": v(70.48, 18.78) * mm, "mid": v(73.7, 21.07) * mm, "end": v(75.06, 24.77) * mm});
            skLineSegment(sketch, "E145.13", {"start": v(46.1, 32.33) * mm, "end": v(61.09, 33.03) * mm});
            skLineSegment(sketch, "E145.14", {"start": v(46.1, 32.33) * mm, "end": v(46.1, 25.92) * mm});
            skLineSegment(sketch, "E145.15", {"start": v(46.1, 25.92) * mm, "end": v(50.3, 25.2) * mm});
            skLineSegment(sketch, "E145.16", {"start": v(50.3, 25.2) * mm, "end": v(50.5, 7.47) * mm});
            skLineSegment(sketch, "E145.17", {"start": v(46.1, 7.47) * mm, "end": v(50.5, 7.47) * mm});
            skLineSegment(sketch, "E145.18", {"start": v(46.1, 7.47) * mm, "end": v(46.1, 0.66) * mm});
            skSolve(sketch);
        }
        {
            var Q0;
            Q0=qSketchRegion(id+"F19",true);
            extrude(context, id + "F20", {"entities" : qUnion([Q0]), "endBound" : BoundingType.SYMMETRIC, "depth" : 1 * mm});
        }
        {
            var Q0;
            Q0=qCreatedBy(makeId("Front.planeOp"),FACE);
            var sketch = newSketch(context, id + "F21", { "sketchPlane" : qUnion([Q0])});
            skCircle(sketch, "E146.0", {"center": v(80.2, 7.44) * mm, "radius": 5.38 * mm});
            skCircle(sketch, "E147.0", {"center": v(80.2, 7.44) * mm, "radius": 7.38 * mm});
            skSolve(sketch);
        }
        {
            var Q0;
            Q0=qSketchRegion(id+"F21",true);
            extrude(context, id + "F22", {"entities" : qUnion([Q0]), "endBound" : BoundingType.SYMMETRIC, "depth" : 1 * mm});
        }
        {
            var Q0;
            Q0=makeQuery(id+"F1.opExtrude","SWEPT_BODY",BODY,{"disambiguationData":[OSD([sQuery(id+"F0.wireOp",EDGE,"E0"),sQuery(id+"F0.wireOp",EDGE,"E1"),sQuery(id+"F0.wireOp",EDGE,"E2"),sQuery(id+"F0.wireOp",EDGE,"E3"),sQuery(id+"F0.wireOp",EDGE,"E4"),sQuery(id+"F0.wireOp",EDGE,"E5"),sQuery(id+"F0.wireOp",EDGE,"E6"),sQuery(id+"F0.wireOp",EDGE,"E7.filletArc"),sQuery(id+"F0.wireOp",EDGE,"E8.filletArc"),sQuery(id+"F0.wireOp",EDGE,"E9"),sQuery(id+"F0.wireOp",EDGE,"E10.filletArc"),sQuery(id+"F0.wireOp",EDGE,"E11.filletArc")])]});
            deleteBodies(context, id + "F23", {"entities" : qUnion([Q0])});
        }
        {
            var Q0;
            Q0=makeQuery(id+"F6.opExtrude","SWEPT_BODY",BODY,{"disambiguationData":[OSD([sQuery(id+"F5.wireOp",EDGE,"E22"),sQuery(id+"F5.wireOp",EDGE,"E23"),sQuery(id+"F5.wireOp",EDGE,"E24"),sQuery(id+"F5.wireOp",EDGE,"E25"),sQuery(id+"F5.wireOp",EDGE,"E26"),sQuery(id+"F5.wireOp",EDGE,"E27"),sQuery(id+"F5.wireOp",EDGE,"E28"),sQuery(id+"F5.wireOp",EDGE,"E29.trimOffspring"),sQuery(id+"F5.wireOp",EDGE,"E30.trimOffspring"),sQuery(id+"F5.wireOp",EDGE,"E31.trimOffspring"),sQuery(id+"F5.wireOp",EDGE,"E32"),sQuery(id+"F5.wireOp",EDGE,"E33"),sQuery(id+"F5.wireOp",EDGE,"E34"),sQuery(id+"F5.wireOp",EDGE,"E35"),sQuery(id+"F5.wireOp",EDGE,"E36"),sQuery(id+"F5.wireOp",EDGE,"E37"),sQuery(id+"F5.wireOp",EDGE,"E38"),sQuery(id+"F5.wireOp",EDGE,"E39"),sQuery(id+"F5.wireOp",EDGE,"E40"),sQuery(id+"F5.wireOp",EDGE,"E41"),sQuery(id+"F5.wireOp",EDGE,"E42.filletArc"),sQuery(id+"F5.wireOp",EDGE,"E43.filletArc")])]});
            var Q1;
            Q1=makeQuery(id+"F8.opExtrude","SWEPT_BODY",BODY,{"disambiguationData":[OSD([sQuery(id+"F7.wireOp",EDGE,"E44")])]});
            deleteBodies(context, id + "F24", {"entities" : qUnion([Q0, Q1])});
        }
    });
